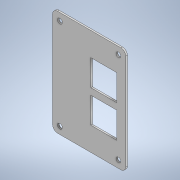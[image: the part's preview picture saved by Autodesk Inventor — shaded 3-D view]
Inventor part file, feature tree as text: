
AUTODESK INVENTOR PART (.ipt)
format: ipt  version: 2021.2 (Build 252289000, 289)  size: 118,272 bytes
history: native  units: mm
features: other x4, reference x3, extrude x1, sketch x1
ambient origin geometry x8: Origin, YZ Plane, XZ Plane, XY Plane, X Axis, Y Axis, Z Axis, Center Point
bodies: Body1 (feature_tree)
feature tree (9):
  other  "Твердое тело1"
  extrude  "Выдавливание1"  Depth=1.0mm TaperAngle=0.0deg
  sketch  "Эскиз1"
  reference  "Ссылка1"
  reference  "Ссылка2"
  reference  "Ссылка3"
  other  "Сборка1"
  other  "plate:1"
  other  "level2_up:1"
